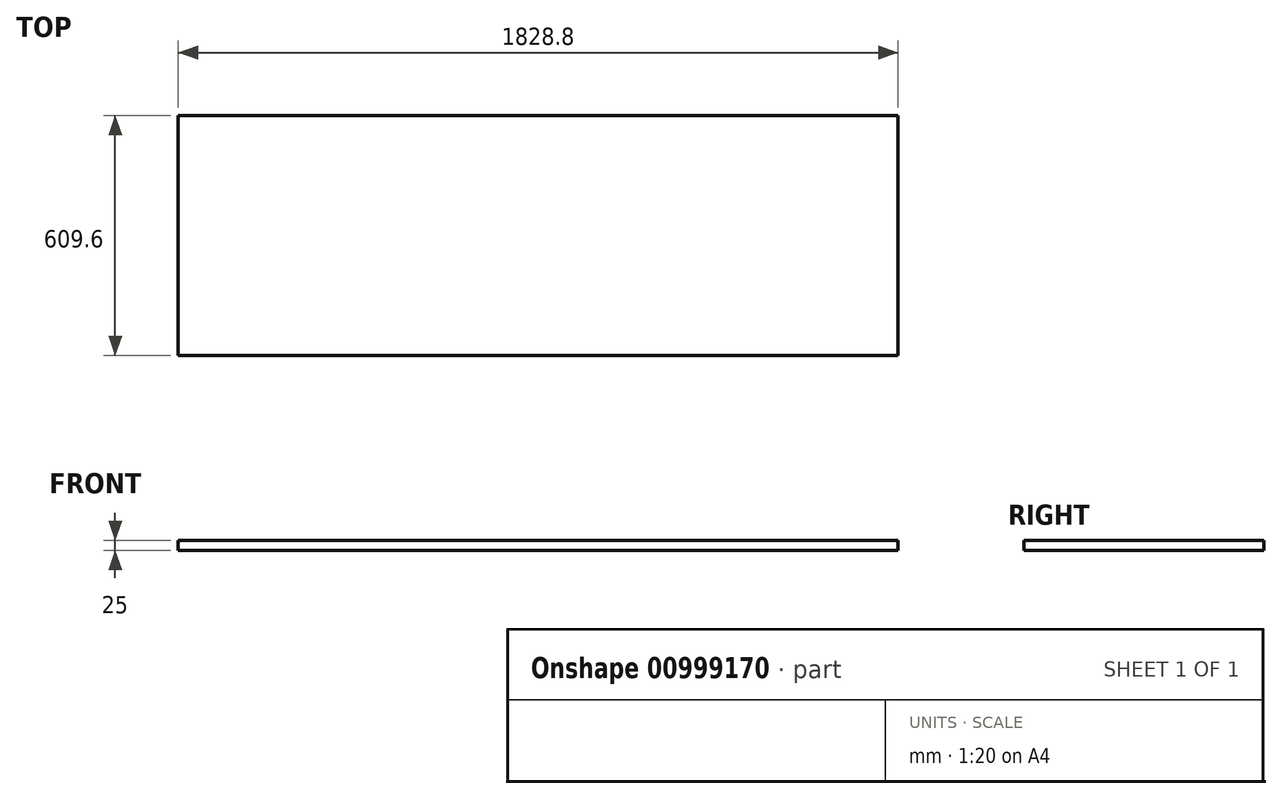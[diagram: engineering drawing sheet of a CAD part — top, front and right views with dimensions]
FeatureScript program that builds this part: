
annotation { "Feature Type Name" : "Feature", "Feature Type Description" : "" }
export const myFeature = defineFeature(function(context is Context, id is Id, definition is map)
    precondition{}
    {
        {
            var Q0;
            Q0=qCreatedBy(makeId("Top.planeOp"),FACE);
            var sketch = newSketch(context, id + "F0", { "sketchPlane" : qUnion([Q0])});
            skLineSegment(sketch, "E0.bottom", {"start": v(914.4, 304.8) * mm, "end": v(-914.4, 304.8) * mm});
            skLineSegment(sketch, "E0.top", {"start": v(914.4, -304.8) * mm, "end": v(-914.4, -304.8) * mm});
            skLineSegment(sketch, "E0.left", {"start": v(914.4, 304.8) * mm, "end": v(914.4, -304.8) * mm});
            skLineSegment(sketch, "E0.right", {"start": v(-914.4, 304.8) * mm, "end": v(-914.4, -304.8) * mm});
            skPoint(sketch, "E0.middle", {"position": v(0, 0) * mm});
            skSolve(sketch);
        }
        {
            var Q0;
            Q0=makeQuery(id+"F0.imprint","IMPRINT",FACE,{"disambiguationData":[TD([[makeQuery(id+"F0.imprint","IMPRINT",EDGE,{"derivedFrom":sQuery(id+"F0.wireOp",EDGE,"E0.bottom")}),1.0]])]});
            extrude(context, id + "F1", {"entities" : qUnion([Q0]), "depth" : 25 * mm, "offsetDistance" : 25 * mm});
        }
    });
